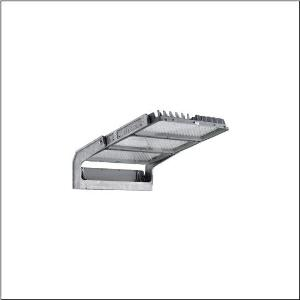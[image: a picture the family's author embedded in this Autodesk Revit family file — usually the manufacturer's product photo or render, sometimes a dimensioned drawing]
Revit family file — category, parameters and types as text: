
# Revit family: floodlight_fl_11_maxi_pro___rs07_5xa779129k02fb_e546
name_source: partatom
category: Lighting Fixtures
units: mm (PartAtom-declared; Revit-internal decimal feet)

## family parameters
Cut with Voids When Loaded = No
Host = Face
Light Source = No
Part Type = Normal
Room Calculation Point = No
Round Connector Dimension = Use Diameter
Shared = No

## types (1)
- --- (1 x LED, 173450 lm, 1400 W, 5700K)
    Apparent Load = 1400 VA
    CIE Flux Codes = 80 93 99 100 99
    Color Rendering = 70
    Color Temperature = 5700K
    Default Elevation = 1800 mm
    Description = Floodlight FL 11  maxi  pro floodlight; light control with lens of PMMA; cover panel of toughened safety glass, transparent; light distribution: RS07, rotationally symmetric direct distribution, LED; colour temperature: 5700K, rated luminous flux: 173.450lm, colour rendering: CRI > 70, light colour: 757; luminous efficacy: 124lm/W; brightness control: DALI 2; with terminal, 5-pole, max. 2.5mm², mains connection: 220..240V/380..400V AC, 50/60Hz, surge voltage resistance: line to ground: 10kV, LED service life up to 100,000h L90. Typical operating time: 1000h per year., ECG replaceable separately, LED unit replaceable without ESD environment, dustproof LED module, dimming range 10..100%; 1400W floodlight with 3x LED unit of diecast aluminium, coated grey; length: 1.003mm / width: 651mm / height: 338mm; mounting bracket, of diecast aluminium, uncoated, natural, equipment: Power, protection rating (complete): IP66; insulation class (complete): insulation class I (protective earthing); certification: CE, ENEC, VDE; ball protection: ball impact resistant, only for outdoor installations in the designated locations, permissible operating ambient temperature: -45..+55°C, permissible storage temperature: -40..+85°Cpackaging unit: 1 piece

Light Distribution: RS07
    Height = 320 mm
    Lamp = 1 x LED
    Lamp Light Flux = 173450 lm
    Lamp Power = 1400 W
    Lamp count = 1
    Length = 1002 mm
    Luminous efficacy = 124 lm/W
    Manufacturer = Siteco
    ModVariant = No
    Model = 5XA779129K02FB
    Mounting Place = Ceiling
    Mounting Type = Surface mounted
    Number of Poles = 1
    OnlyDefault = Yes
    Power Factor = 1
    Product Name = Floodlight FL 11 maxi pro | RS07
    Product group = floodlight | ceiling mounted
    ProductGroupID = 303
    Protection Class = Protection class I
    Protection Degree = IP 66
    RLX_Detail_Level = 1
    RLX_Emergency_Light_Flux = 0 lm
    RLX_Emergency_Type = 0
    RLX_Emergency_Type_DB = No
    RlxData = <blob elided: 40297 chars, md5=02b37348>
    Socket = socket
    Standby Power = 0 W
    System Light Flux = 173450 lm
    System Power = 1400 W
    Type Comments = factory setting: luminous flux: 100 % | dim-lin: 254 | 955 mA
    Type Image = l_1356210.jpg
    URL = http://relux.com
    VarID = @adj_038843
    Voltage = 0 V
    Weight = 0.00 kg
    Width = 655 mm

## geometry (parser evidence)
native form markers: Blend x4, Sweep x13
no freeform markers — native parametric forms only
